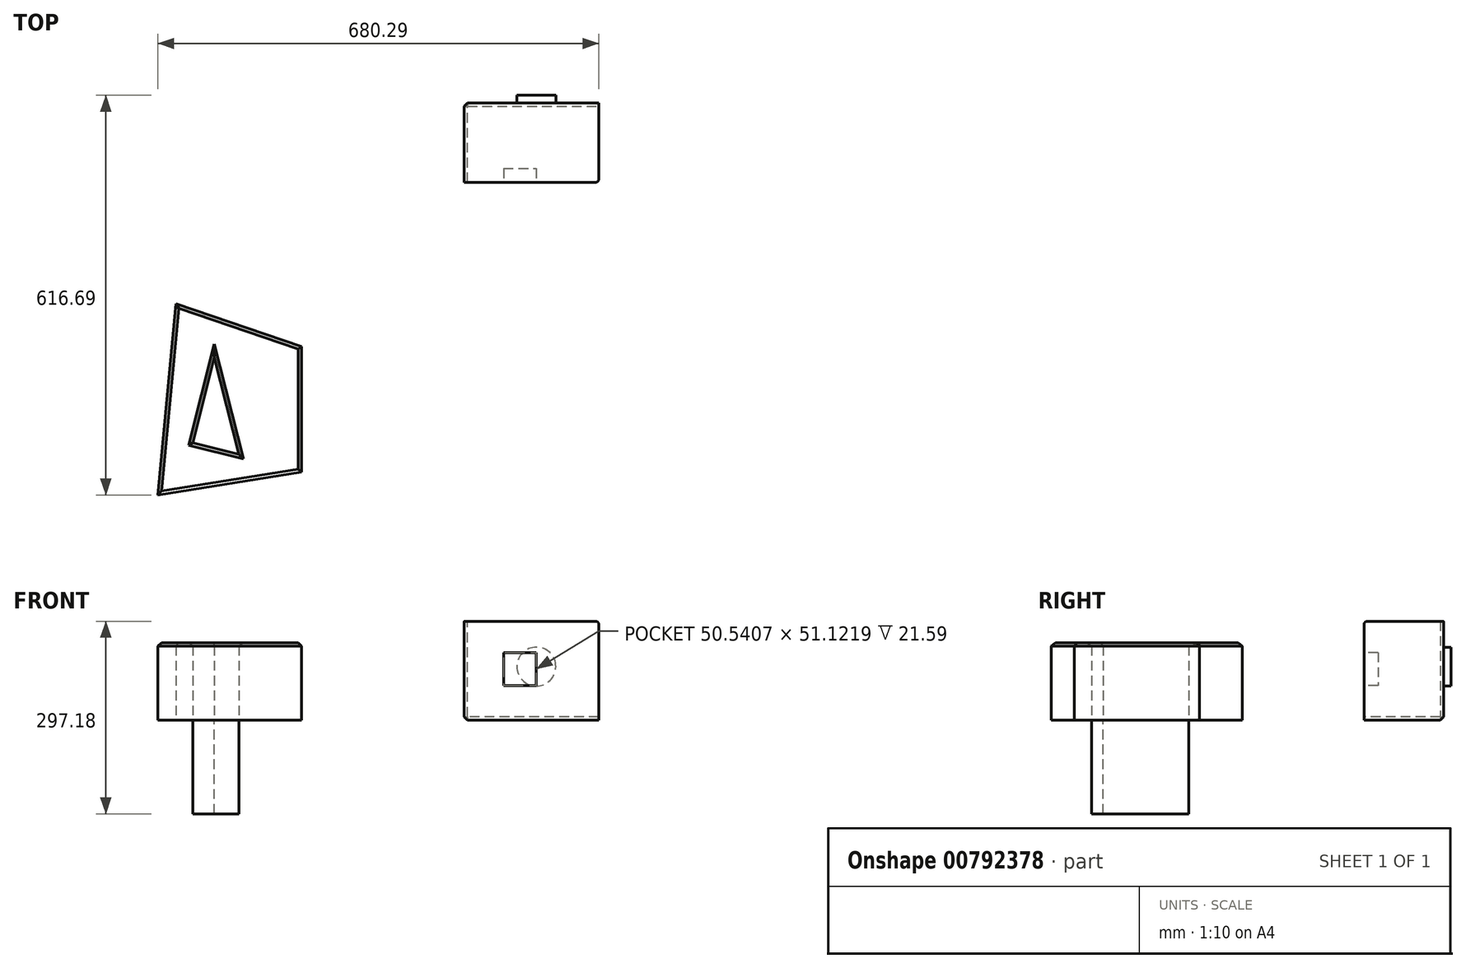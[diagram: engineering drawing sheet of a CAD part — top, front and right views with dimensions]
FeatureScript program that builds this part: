
annotation { "Feature Type Name" : "Feature", "Feature Type Description" : "" }
export const myFeature = defineFeature(function(context is Context, id is Id, definition is map)
    precondition{}
    {
        {
            var Q0;
            Q0=qCreatedBy(makeId("Top.planeOp"),FACE);
            var sketch = newSketch(context, id + "F0", { "sketchPlane" : qUnion([Q0])});
            skCircle(sketch, "E0", {"center": v(-311.54, 245.35) * mm, "radius": 63.5 * mm});
            skLineSegment(sketch, "E1.bottom", {"start": v(108.5, 232.64) * mm, "end": v(316.03, 232.64) * mm});
            skLineSegment(sketch, "E1.top", {"start": v(108.5, 110) * mm, "end": v(316.03, 110) * mm});
            skLineSegment(sketch, "E1.left", {"start": v(108.5, 232.64) * mm, "end": v(108.5, 110) * mm});
            skLineSegment(sketch, "E1.right", {"start": v(316.03, 232.64) * mm, "end": v(316.03, 110) * mm});
            skLineSegment(sketch, "E2", {"start": v(-335.96, -77.57) * mm, "end": v(-142.58, -143.6) * mm});
            skLineSegment(sketch, "E3", {"start": v(-142.58, -143.6) * mm, "end": v(-142.58, -336.98) * mm});
            skLineSegment(sketch, "E4", {"start": v(-142.58, -336.98) * mm, "end": v(-364.26, -372.36) * mm});
            skLineSegment(sketch, "E5", {"start": v(-364.26, -372.36) * mm, "end": v(-335.96, -77.57) * mm});
            skLineSegment(sketch, "E6", {"start": v(-277, -160.1) * mm, "end": v(-310.02, -292.17) * mm});
            skLineSegment(sketch, "E7", {"start": v(-310.02, -292.17) * mm, "end": v(-239, -309.93) * mm});
            skLineSegment(sketch, "E8", {"start": v(-239, -309.93) * mm, "end": v(-277, -160.1) * mm});
            skSolve(sketch);
        }
        {
            var Q0;
            Q0=makeQuery(id+"F0.imprint","IMPRINT",FACE,{"disambiguationData":[TD([[makeQuery(id+"F0.imprint","IMPRINT",EDGE,{"derivedFrom":sQuery(id+"F0.wireOp",EDGE,"E1.bottom")}),-1.0]])]});
            extrude(context, id + "F1", {"entities" : qUnion([Q0]), "depth" : 152.4 * mm, "offsetDistance" : 25.4 * mm});
        }
        {
            var Q0;
            Q0=sQuery(id+"F0.wireOp",EDGE,"E0");
            extrude(context, id + "F2", {"bodyType" : ToolBodyType.SURFACE, "surfaceEntities" : qUnion([Q0]), "depth" : 152.4 * mm, "offsetDistance" : 25.4 * mm});
        }
        {
            var Q0;
            Q0=makeQuery(id+"F0.imprint","IMPRINT",FACE,{"disambiguationData":[TD([[makeQuery(id+"F0.imprint","IMPRINT",EDGE,{"derivedFrom":sQuery(id+"F0.wireOp",EDGE,"E6")}),1.0]])]});
            extrude(context, id + "F3", {"entities" : qUnion([Q0]), "oppositeDirection" : true, "depth" : 144.78 * mm, "offsetDistance" : 25.4 * mm});
        }
        {
            var Q0;
            Q0=makeQuery(id+"F0.imprint","IMPRINT",FACE,{"disambiguationData":[TD([[makeQuery(id+"F0.imprint","IMPRINT",EDGE,{"derivedFrom":sQuery(id+"F0.wireOp",EDGE,"E2")}),-1.0]])]});
            extrude(context, id + "F4", {"entities" : qUnion([Q0]), "depth" : 119.38 * mm, "offsetDistance" : 25.4 * mm});
        }
        {
            var Q0;
            Q0=makeQuery(id+"F1.opExtrude","CAP_EDGE",EDGE,{"disambiguationData":[OSD([sQuery(id+"F0.wireOp",EDGE,"E1.top")])],"isStart":false});
            var Q1;
            Q1=makeQuery(id+"F1.opExtrude","CAP_EDGE",EDGE,{"disambiguationData":[OSD([sQuery(id+"F0.wireOp",EDGE,"E1.right")])],"isStart":false});
            var Q2;
            Q2=makeQuery(id+"F1.opExtrude","SWEPT_EDGE",EDGE,{"disambiguationData":[OSD([sQuery(id+"F0.wireOp",EDGE,"E1.top"),sQuery(id+"F0.wireOp",EDGE,"E1.right")])]});
            fillet(context, id + "F5", {"entities" : qUnion([Q0, Q1, Q2]), "radius" : 5.08 * mm, "tangentPropagation" : true, "allowEdgeOverflow" : false});
        }
        {
            var Q0;
            Q0=makeQuery(id+"F1.opExtrude","SWEPT_EDGE",EDGE,{"disambiguationData":[OSD([sQuery(id+"F0.wireOp",EDGE,"E1.bottom"),sQuery(id+"F0.wireOp",EDGE,"E1.left")])]});
            var Q1;
            Q1=makeQuery(id+"F1.opExtrude","CAP_EDGE",EDGE,{"disambiguationData":[OSD([sQuery(id+"F0.wireOp",EDGE,"E1.bottom")])],"isStart":true});
            var Q2;
            Q2=makeQuery(id+"F1.opExtrude","CAP_EDGE",EDGE,{"disambiguationData":[OSD([sQuery(id+"F0.wireOp",EDGE,"E1.left")])],"isStart":true});
            chamfer(context, id + "F6", {"entities" : qUnion([Q0, Q1, Q2]), "width" : 5.08 * mm, "tangentPropagation" : true});
        }
        {
            var Q0;
            Q0=makeQuery(id+"F4.opExtrude","CAP_FACE",FACE,{"disambiguationData":[OSD([sQuery(id+"F0.wireOp",EDGE,"E2"),sQuery(id+"F0.wireOp",EDGE,"E3"),sQuery(id+"F0.wireOp",EDGE,"E4"),sQuery(id+"F0.wireOp",EDGE,"E5"),sQuery(id+"F0.wireOp",EDGE,"E6"),sQuery(id+"F0.wireOp",EDGE,"E7"),sQuery(id+"F0.wireOp",EDGE,"E8")])],"isStart":false});
            chamfer(context, id + "F7", {"entities" : qUnion([Q0]), "width" : 5.08 * mm, "tangentPropagation" : true});
        }
        {
            var Q0;
            Q0=makeQuery(id+"F1.opExtrude","SWEPT_FACE",FACE,{"disambiguationData":[OSD([sQuery(id+"F0.wireOp",EDGE,"E1.bottom")])]});
            var sketch = newSketch(context, id + "F8", { "sketchPlane" : qUnion([Q0])});
            skCircle(sketch, "E9", {"center": v(-219.8, 82.35) * mm, "radius": 30.06 * mm});
            skSolve(sketch);
        }
        {
            var Q0;
            Q0=makeQuery(id+"F8.imprint","IMPRINT",FACE,{"disambiguationData":[TD([[makeQuery(id+"F8.imprint","IMPRINT",EDGE,{"derivedFrom":sQuery(id+"F8.wireOp",EDGE,"E9")}),1.0]])]});
            extrude(context, id + "F9", {"entities" : qUnion([Q0]), "operationType" : NewBodyOperationType.ADD, "depth" : 11.68 * mm, "offsetDistance" : 25.4 * mm});
        }
        {
            var Q0;
            Q0=makeQuery(id+"F1.opExtrude","SWEPT_FACE",FACE,{"disambiguationData":[OSD([sQuery(id+"F0.wireOp",EDGE,"E1.top")])]});
            var sketch = newSketch(context, id + "F10", { "sketchPlane" : qUnion([Q0])});
            skLineSegment(sketch, "E10.bottom", {"start": v(169.22, 104.2) * mm, "end": v(219.76, 104.2) * mm});
            skLineSegment(sketch, "E10.top", {"start": v(169.22, 53.07) * mm, "end": v(219.76, 53.07) * mm});
            skLineSegment(sketch, "E10.left", {"start": v(169.22, 104.2) * mm, "end": v(169.22, 53.07) * mm});
            skLineSegment(sketch, "E10.right", {"start": v(219.76, 104.2) * mm, "end": v(219.76, 53.07) * mm});
            skSolve(sketch);
        }
        {
            var Q0;
            Q0=makeQuery(id+"F10.imprint","IMPRINT",FACE,{"disambiguationData":[TD([[makeQuery(id+"F10.imprint","IMPRINT",EDGE,{"derivedFrom":sQuery(id+"F10.wireOp",EDGE,"E10.bottom")}),-1.0]])]});
            extrude(context, id + "F11", {"entities" : qUnion([Q0]), "operationType" : NewBodyOperationType.REMOVE, "oppositeDirection" : true, "depth" : 21.59 * mm, "offsetDistance" : 25.4 * mm});
        }
    });
